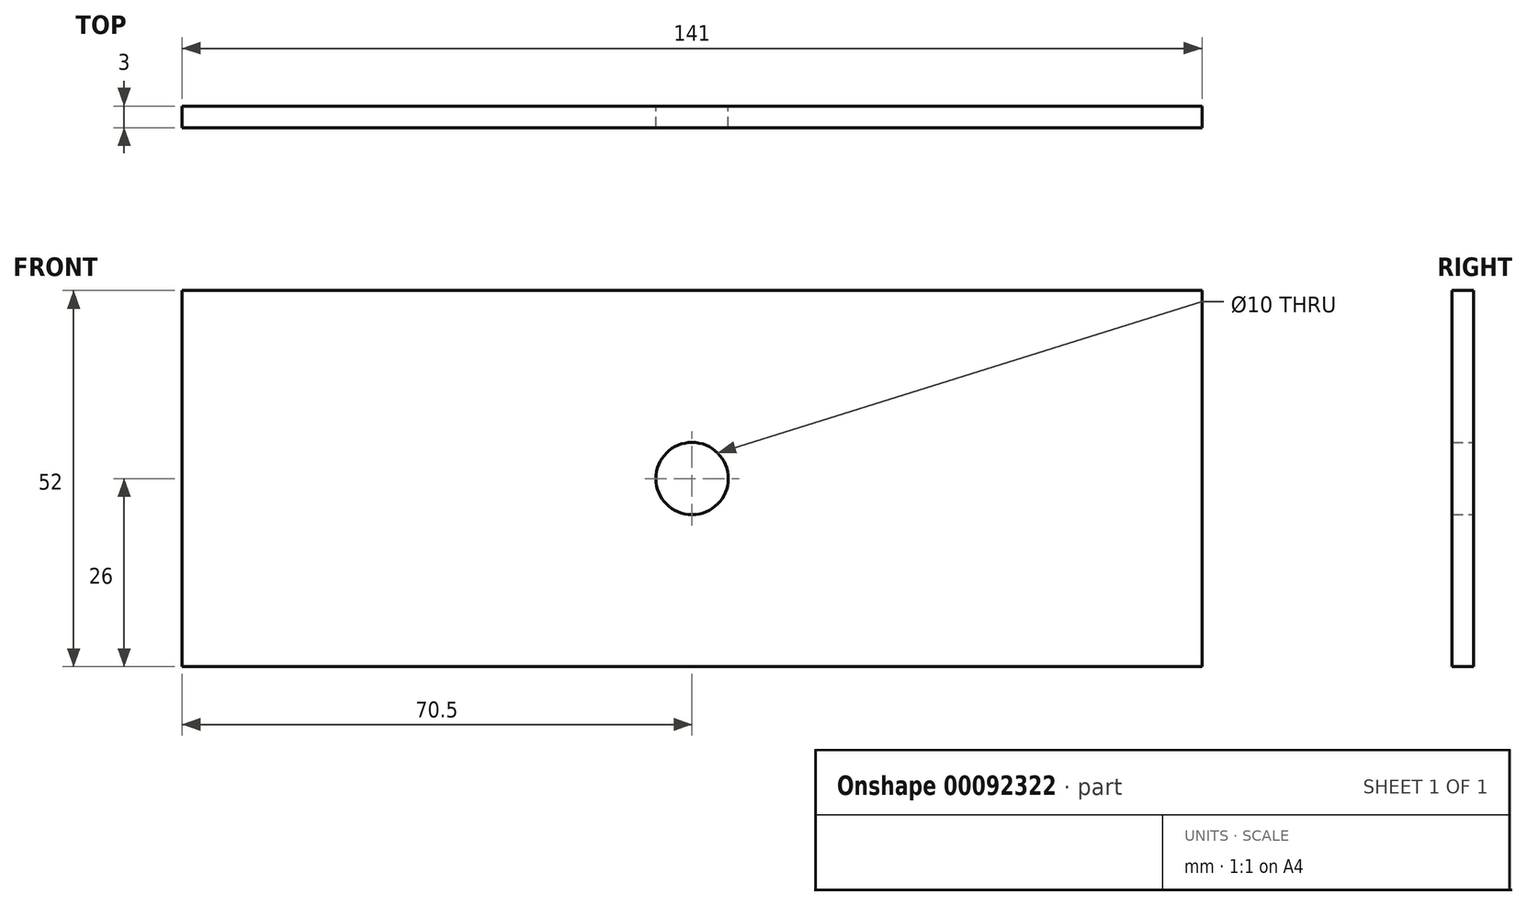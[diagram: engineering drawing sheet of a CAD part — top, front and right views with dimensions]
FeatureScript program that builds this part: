
annotation { "Feature Type Name" : "Feature", "Feature Type Description" : "" }
export const myFeature = defineFeature(function(context is Context, id is Id, definition is map)
    precondition{}
    {
        {
            var Q0;
            Q0=qCreatedBy(makeId("Front.planeOp"),FACE);
            var sketch = newSketch(context, id + "F0", { "sketchPlane" : qUnion([Q0])});
            skLineSegment(sketch, "E0.bottom", {"start": v(-70.5, 26) * mm, "end": v(70.5, 26) * mm});
            skLineSegment(sketch, "E0.top", {"start": v(-70.5, -26) * mm, "end": v(70.5, -26) * mm});
            skLineSegment(sketch, "E0.left", {"start": v(-70.5, 26) * mm, "end": v(-70.5, -26) * mm});
            skLineSegment(sketch, "E0.right", {"start": v(70.5, 26) * mm, "end": v(70.5, -26) * mm});
            skSolve(sketch);
        }
        {
            var Q0;
            Q0=makeQuery(id+"F0.imprint","IMPRINT",FACE,{"disambiguationData":[TD([[makeQuery(id+"F0.imprint","IMPRINT",EDGE,{"derivedFrom":sQuery(id+"F0.wireOp",EDGE,"E0.bottom")}),-1.0]])]});
            extrude(context, id + "F1", {"entities" : qUnion([Q0]), "endBound" : BoundingType.SYMMETRIC, "depth" : 3 * mm});
        }
        {
            var Q0;
            Q0=makeQuery(id+"F1.opExtrude","CAP_FACE",FACE,{"disambiguationData":[OSD([sQuery(id+"F0.wireOp",EDGE,"E0.bottom"),sQuery(id+"F0.wireOp",EDGE,"E0.top"),sQuery(id+"F0.wireOp",EDGE,"E0.left"),sQuery(id+"F0.wireOp",EDGE,"E0.right")])],"isStart":true});
            var sketch = newSketch(context, id + "F2", { "sketchPlane" : qUnion([Q0])});
            skCircle(sketch, "E1", {"center": v(0, 0) * mm, "radius": 5 * mm});
            skSolve(sketch);
        }
        {
            var Q0;
            Q0 = qSketchRegion(id + "F2", true);
            extrude(context, id + "F3", {"entities" : qUnion([Q0]), "operationType" : NewBodyOperationType.REMOVE, "endBound" : BoundingType.UP_TO_NEXT, "oppositeDirection" : true, "depth" : 25 * mm});
        }
    });
